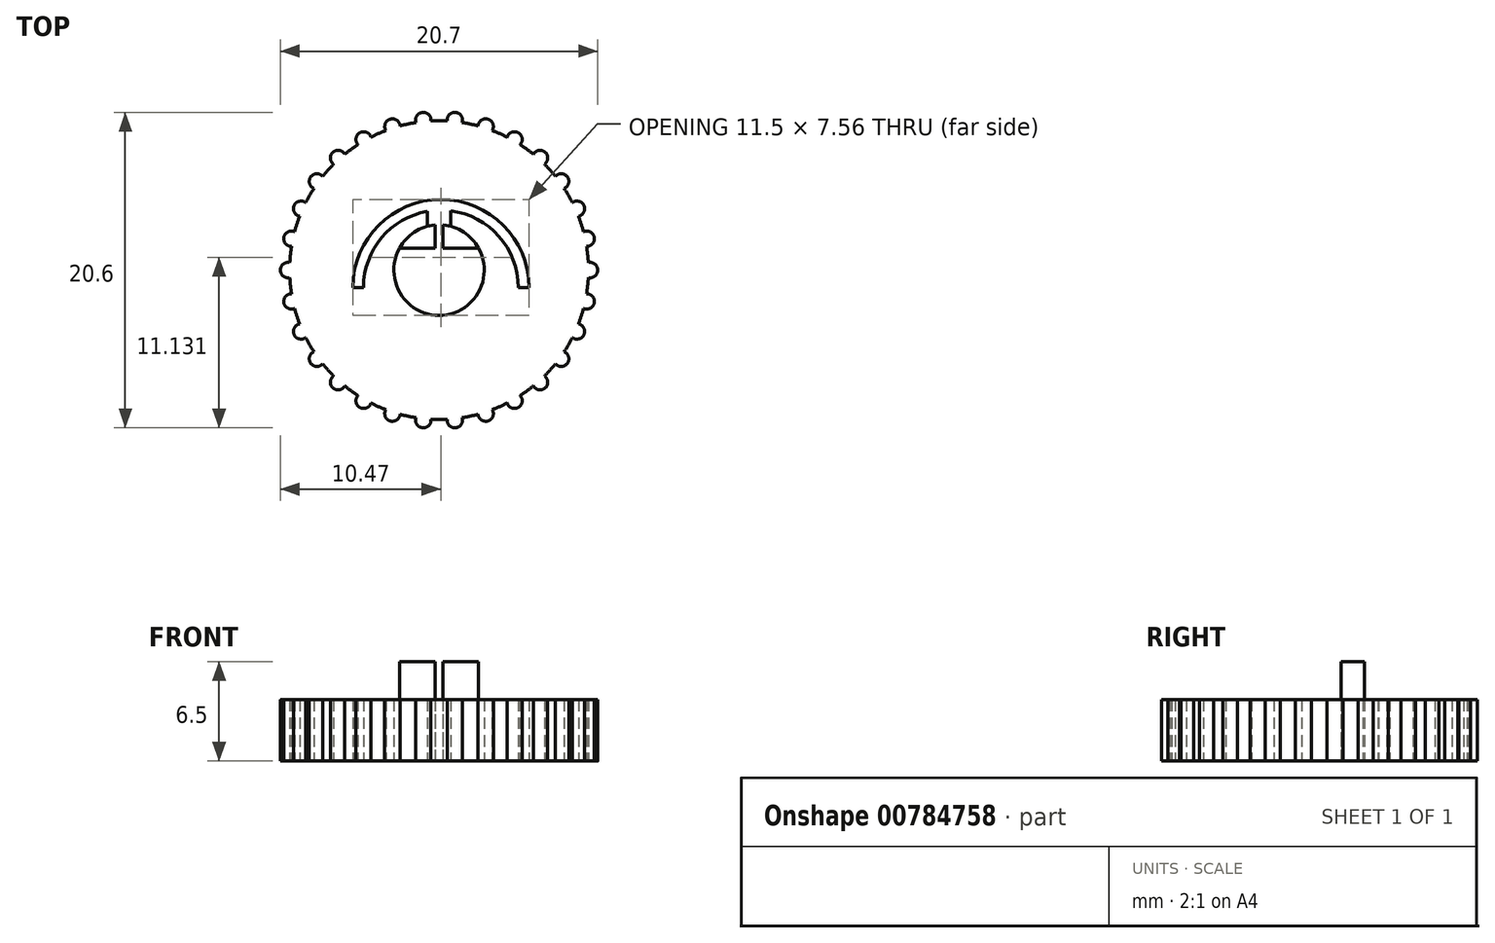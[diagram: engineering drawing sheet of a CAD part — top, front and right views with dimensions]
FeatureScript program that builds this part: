
annotation { "Feature Type Name" : "Feature", "Feature Type Description" : "" }
export const myFeature = defineFeature(function(context is Context, id is Id, definition is map)
    precondition{}
    {
        {
            var Q0;
            Q0=qCreatedBy(makeId("Top.planeOp"),FACE);
            var sketch = newSketch(context, id + "F0", { "sketchPlane" : qUnion([Q0])});
            skArc(sketch, "E0", {"start": v(-2.58, 1.43) * mm, "mid": v(0, -2.95) * mm, "end": v(2.58, 1.43) * mm});
            skArc(sketch, "E1", {"start": v(-0.75, 3.84) * mm, "mid": v(-3.75, 2.11) * mm, "end": v(-4.93, -1.14) * mm});
            skArc(sketch, "E2", {"start": v(5.87, -1.14) * mm, "mid": v(0.12, 4.61) * mm, "end": v(-5.63, -1.14) * mm});
            skArc(sketch, "E3", {"start": v(-9.74, -0.49) * mm, "mid": v(-9.7, -1.02) * mm, "end": v(-9.63, -1.55) * mm});
            skLineSegment(sketch, "E4", {"start": v(-5.63, -1.14) * mm, "end": v(-4.93, -1.14) * mm});
            skLineSegment(sketch, "E5.trimOffspring", {"start": v(5.17, -1.14) * mm, "end": v(5.87, -1.14) * mm});
            skArc(sketch, "E6.trimOffspring", {"start": v(5.17, -1.14) * mm, "mid": v(3.9, 2.2) * mm, "end": v(0.75, 3.87) * mm});
            skArc(sketch, "E7", {"start": v(-9.74, 0.49) * mm, "mid": v(-10.35, 0) * mm, "end": v(-9.74, -0.49) * mm});
            skArc(sketch, "E8.1.0", {"start": v(-9.63, -1.55) * mm, "mid": v(-10.12, -2.15) * mm, "end": v(-9.42, -2.5) * mm});
            skArc(sketch, "E8.2.0", {"start": v(-9.1, -3.52) * mm, "mid": v(-9.46, -4.21) * mm, "end": v(-8.7, -4.4) * mm});
            skArc(sketch, "E8.3.0", {"start": v(-8.16, -5.33) * mm, "mid": v(-8.37, -6.08) * mm, "end": v(-7.6, -6.12) * mm});
            skArc(sketch, "E8.4.0", {"start": v(-6.88, -6.91) * mm, "mid": v(-6.93, -7.7) * mm, "end": v(-6.15, -7.56) * mm});
            skArc(sketch, "E8.5.0", {"start": v(-5.3, -8.19) * mm, "mid": v(-5.18, -8.96) * mm, "end": v(-4.45, -8.68) * mm});
            skArc(sketch, "E8.6.0", {"start": v(-3.47, -9.11) * mm, "mid": v(-3.2, -9.84) * mm, "end": v(-2.55, -9.41) * mm});
            skArc(sketch, "E8.7.0", {"start": v(-1.5, -9.63) * mm, "mid": v(-1.08, -10.3) * mm, "end": v(-0.53, -9.74) * mm});
            skArc(sketch, "E8.8.0", {"start": v(0.53, -9.74) * mm, "mid": v(1.08, -10.3) * mm, "end": v(1.5, -9.63) * mm});
            skArc(sketch, "E8.9.0", {"start": v(2.55, -9.41) * mm, "mid": v(3.2, -9.84) * mm, "end": v(3.47, -9.11) * mm});
            skArc(sketch, "E8.10.0", {"start": v(4.45, -8.68) * mm, "mid": v(5.18, -8.96) * mm, "end": v(5.3, -8.19) * mm});
            skArc(sketch, "E8.11.0", {"start": v(6.15, -7.56) * mm, "mid": v(6.93, -7.7) * mm, "end": v(6.88, -6.91) * mm});
            skArc(sketch, "E8.12.0", {"start": v(7.6, -6.12) * mm, "mid": v(8.37, -6.08) * mm, "end": v(8.16, -5.33) * mm});
            skArc(sketch, "E8.13.0", {"start": v(8.7, -4.4) * mm, "mid": v(9.46, -4.21) * mm, "end": v(9.1, -3.52) * mm});
            skArc(sketch, "E8.14.0", {"start": v(9.42, -2.5) * mm, "mid": v(10.12, -2.15) * mm, "end": v(9.63, -1.55) * mm});
            skArc(sketch, "E8.15.0", {"start": v(9.74, -0.49) * mm, "mid": v(10.35, 0) * mm, "end": v(9.74, 0.49) * mm});
            skArc(sketch, "E8.16.0", {"start": v(9.63, 1.55) * mm, "mid": v(10.12, 2.15) * mm, "end": v(9.42, 2.5) * mm});
            skArc(sketch, "E8.17.0", {"start": v(9.1, 3.52) * mm, "mid": v(9.46, 4.21) * mm, "end": v(8.7, 4.4) * mm});
            skArc(sketch, "E8.18.0", {"start": v(8.16, 5.33) * mm, "mid": v(8.37, 6.08) * mm, "end": v(7.6, 6.12) * mm});
            skArc(sketch, "E8.19.0", {"start": v(6.88, 6.91) * mm, "mid": v(6.93, 7.7) * mm, "end": v(6.15, 7.56) * mm});
            skArc(sketch, "E8.20.0", {"start": v(5.3, 8.19) * mm, "mid": v(5.18, 8.96) * mm, "end": v(4.45, 8.68) * mm});
            skArc(sketch, "E8.21.0", {"start": v(3.47, 9.11) * mm, "mid": v(3.2, 9.84) * mm, "end": v(2.55, 9.41) * mm});
            skArc(sketch, "E8.22.0", {"start": v(1.5, 9.63) * mm, "mid": v(1.08, 10.3) * mm, "end": v(0.53, 9.74) * mm});
            skArc(sketch, "E8.23.0", {"start": v(-0.53, 9.74) * mm, "mid": v(-1.08, 10.3) * mm, "end": v(-1.5, 9.63) * mm});
            skArc(sketch, "E8.24.0", {"start": v(-2.55, 9.41) * mm, "mid": v(-3.2, 9.84) * mm, "end": v(-3.47, 9.11) * mm});
            skArc(sketch, "E8.25.0", {"start": v(-4.45, 8.68) * mm, "mid": v(-5.18, 8.96) * mm, "end": v(-5.3, 8.19) * mm});
            skArc(sketch, "E8.26.0", {"start": v(-6.15, 7.56) * mm, "mid": v(-6.93, 7.7) * mm, "end": v(-6.88, 6.91) * mm});
            skArc(sketch, "E8.27.0", {"start": v(-7.6, 6.12) * mm, "mid": v(-8.37, 6.08) * mm, "end": v(-8.16, 5.33) * mm});
            skArc(sketch, "E8.28.0", {"start": v(-8.7, 4.4) * mm, "mid": v(-9.46, 4.21) * mm, "end": v(-9.1, 3.52) * mm});
            skArc(sketch, "E8.29.0", {"start": v(-9.42, 2.5) * mm, "mid": v(-10.12, 2.15) * mm, "end": v(-9.63, 1.55) * mm});
            skArc(sketch, "E9.trimOffspring", {"start": v(-9.63, 1.55) * mm, "mid": v(-9.7, 1.02) * mm, "end": v(-9.74, 0.49) * mm});
            skArc(sketch, "E10.trimOffspring", {"start": v(-9.1, 3.52) * mm, "mid": v(-9.27, 3.01) * mm, "end": v(-9.42, 2.5) * mm});
            skArc(sketch, "E11.trimOffspring", {"start": v(-8.16, 5.33) * mm, "mid": v(-8.44, 4.88) * mm, "end": v(-8.7, 4.4) * mm});
            skArc(sketch, "E12.trimOffspring", {"start": v(-6.88, 6.91) * mm, "mid": v(-7.25, 6.52) * mm, "end": v(-7.6, 6.12) * mm});
            skArc(sketch, "E13.trimOffspring", {"start": v(-5.3, 8.19) * mm, "mid": v(-5.73, 7.89) * mm, "end": v(-6.15, 7.56) * mm});
            skArc(sketch, "E14.trimOffspring", {"start": v(-3.47, 9.11) * mm, "mid": v(-3.97, 8.9) * mm, "end": v(-4.45, 8.68) * mm});
            skArc(sketch, "E15.trimOffspring", {"start": v(-1.5, 9.63) * mm, "mid": v(-2.03, 9.54) * mm, "end": v(-2.55, 9.41) * mm});
            skArc(sketch, "E16.trimOffspring", {"start": v(0.53, 9.74) * mm, "mid": v(0, 9.75) * mm, "end": v(-0.53, 9.74) * mm});
            skArc(sketch, "E17.trimOffspring", {"start": v(2.55, 9.41) * mm, "mid": v(2.03, 9.54) * mm, "end": v(1.5, 9.63) * mm});
            skArc(sketch, "E18.trimOffspring", {"start": v(4.45, 8.68) * mm, "mid": v(3.97, 8.9) * mm, "end": v(3.47, 9.11) * mm});
            skArc(sketch, "E19.trimOffspring", {"start": v(6.15, 7.56) * mm, "mid": v(5.73, 7.89) * mm, "end": v(5.3, 8.19) * mm});
            skArc(sketch, "E20.trimOffspring", {"start": v(7.6, 6.12) * mm, "mid": v(7.25, 6.52) * mm, "end": v(6.88, 6.91) * mm});
            skArc(sketch, "E21.trimOffspring", {"start": v(8.7, 4.4) * mm, "mid": v(8.44, 4.87) * mm, "end": v(8.16, 5.33) * mm});
            skArc(sketch, "E22.trimOffspring", {"start": v(9.42, 2.5) * mm, "mid": v(9.27, 3.01) * mm, "end": v(9.1, 3.52) * mm});
            skArc(sketch, "E23.trimOffspring", {"start": v(9.74, 0.49) * mm, "mid": v(9.7, 1.02) * mm, "end": v(9.63, 1.55) * mm});
            skArc(sketch, "E24.trimOffspring", {"start": v(9.63, -1.55) * mm, "mid": v(9.7, -1.02) * mm, "end": v(9.74, -0.49) * mm});
            skArc(sketch, "E25.trimOffspring", {"start": v(8.16, -5.33) * mm, "mid": v(8.44, -4.87) * mm, "end": v(8.7, -4.4) * mm});
            skArc(sketch, "E26.trimOffspring", {"start": v(6.88, -6.91) * mm, "mid": v(7.25, -6.52) * mm, "end": v(7.6, -6.12) * mm});
            skArc(sketch, "E27.trimOffspring", {"start": v(5.3, -8.19) * mm, "mid": v(5.73, -7.89) * mm, "end": v(6.15, -7.56) * mm});
            skArc(sketch, "E28.trimOffspring", {"start": v(3.47, -9.11) * mm, "mid": v(3.97, -8.9) * mm, "end": v(4.45, -8.68) * mm});
            skArc(sketch, "E29.trimOffspring", {"start": v(1.5, -9.63) * mm, "mid": v(2.03, -9.54) * mm, "end": v(2.55, -9.41) * mm});
            skArc(sketch, "E30.trimOffspring", {"start": v(-0.53, -9.74) * mm, "mid": v(0, -9.75) * mm, "end": v(0.53, -9.74) * mm});
            skArc(sketch, "E31.trimOffspring", {"start": v(-2.55, -9.41) * mm, "mid": v(-2.03, -9.54) * mm, "end": v(-1.5, -9.63) * mm});
            skArc(sketch, "E32.trimOffspring", {"start": v(-4.45, -8.68) * mm, "mid": v(-3.97, -8.9) * mm, "end": v(-3.47, -9.11) * mm});
            skArc(sketch, "E33.trimOffspring", {"start": v(-6.15, -7.56) * mm, "mid": v(-5.73, -7.89) * mm, "end": v(-5.3, -8.19) * mm});
            skArc(sketch, "E34.trimOffspring", {"start": v(-7.6, -6.12) * mm, "mid": v(-7.25, -6.52) * mm, "end": v(-6.88, -6.91) * mm});
            skArc(sketch, "E35.trimOffspring", {"start": v(-8.7, -4.4) * mm, "mid": v(-8.44, -4.88) * mm, "end": v(-8.16, -5.33) * mm});
            skArc(sketch, "E36.trimOffspring", {"start": v(-9.42, -2.5) * mm, "mid": v(-9.27, -3.01) * mm, "end": v(-9.1, -3.52) * mm});
            skLineSegment(sketch, "E37.trimOffspring", {"start": v(-2.58, 1.43) * mm, "end": v(-0.75, 1.43) * mm});
            skLineSegment(sketch, "E38", {"start": v(-0.75, 3.84) * mm, "end": v(-0.75, 1.43) * mm});
            skLineSegment(sketch, "E39", {"start": v(0.75, 3.87) * mm, "end": v(0.75, 1.43) * mm});
            skLineSegment(sketch, "E40.trimOffspring", {"start": v(0.75, 1.43) * mm, "end": v(2.58, 1.43) * mm});
            skArc(sketch, "E41.trimOffspring", {"start": v(9.1, -3.52) * mm, "mid": v(9.27, -3.01) * mm, "end": v(9.42, -2.5) * mm});
            skSolve(sketch);
        }
        {
            var Q0;
            Q0=makeQuery(id+"F0.imprint","IMPRINT",FACE,{"disambiguationData":[TD([[makeQuery(id+"F0.imprint","IMPRINT",EDGE,{"derivedFrom":sQuery(id+"F0.wireOp",EDGE,"E0")}),-1.0]])]});
            extrude(context, id + "F1", {"entities" : qUnion([Q0]), "depth" : 4 * mm, "offsetDistance" : 25 * mm});
        }
        {
            var Q0;
            Q0=makeQuery(id+"F1.opExtrude","CAP_FACE",FACE,{"disambiguationData":[OSD([sQuery(id+"F0.wireOp",EDGE,"E0"),sQuery(id+"F0.wireOp",EDGE,"E1"),sQuery(id+"F0.wireOp",EDGE,"E2"),sQuery(id+"F0.wireOp",EDGE,"E3"),sQuery(id+"F0.wireOp",EDGE,"E4"),sQuery(id+"F0.wireOp",EDGE,"E5.trimOffspring"),sQuery(id+"F0.wireOp",EDGE,"E6.trimOffspring"),sQuery(id+"F0.wireOp",EDGE,"E7"),sQuery(id+"F0.wireOp",EDGE,"E8.1.0"),sQuery(id+"F0.wireOp",EDGE,"E8.2.0"),sQuery(id+"F0.wireOp",EDGE,"E8.3.0"),sQuery(id+"F0.wireOp",EDGE,"E8.4.0"),sQuery(id+"F0.wireOp",EDGE,"E8.5.0"),sQuery(id+"F0.wireOp",EDGE,"E8.6.0"),sQuery(id+"F0.wireOp",EDGE,"E8.7.0"),sQuery(id+"F0.wireOp",EDGE,"E8.8.0"),sQuery(id+"F0.wireOp",EDGE,"E8.9.0"),sQuery(id+"F0.wireOp",EDGE,"E8.10.0"),sQuery(id+"F0.wireOp",EDGE,"E8.11.0"),sQuery(id+"F0.wireOp",EDGE,"E8.12.0"),sQuery(id+"F0.wireOp",EDGE,"E8.14.0"),sQuery(id+"F0.wireOp",EDGE,"E8.15.0"),sQuery(id+"F0.wireOp",EDGE,"E8.16.0"),sQuery(id+"F0.wireOp",EDGE,"E8.17.0"),sQuery(id+"F0.wireOp",EDGE,"E8.18.0"),sQuery(id+"F0.wireOp",EDGE,"E8.19.0"),sQuery(id+"F0.wireOp",EDGE,"E8.20.0"),sQuery(id+"F0.wireOp",EDGE,"E8.21.0"),sQuery(id+"F0.wireOp",EDGE,"E8.22.0"),sQuery(id+"F0.wireOp",EDGE,"E8.23.0"),sQuery(id+"F0.wireOp",EDGE,"E8.24.0"),sQuery(id+"F0.wireOp",EDGE,"E8.25.0"),sQuery(id+"F0.wireOp",EDGE,"E8.26.0"),sQuery(id+"F0.wireOp",EDGE,"E8.27.0"),sQuery(id+"F0.wireOp",EDGE,"E8.28.0"),sQuery(id+"F0.wireOp",EDGE,"E8.29.0"),sQuery(id+"F0.wireOp",EDGE,"E9.trimOffspring"),sQuery(id+"F0.wireOp",EDGE,"E10.trimOffspring"),sQuery(id+"F0.wireOp",EDGE,"E11.trimOffspring"),sQuery(id+"F0.wireOp",EDGE,"E12.trimOffspring"),sQuery(id+"F0.wireOp",EDGE,"E13.trimOffspring"),sQuery(id+"F0.wireOp",EDGE,"E14.trimOffspring"),sQuery(id+"F0.wireOp",EDGE,"E15.trimOffspring"),sQuery(id+"F0.wireOp",EDGE,"E16.trimOffspring"),sQuery(id+"F0.wireOp",EDGE,"E17.trimOffspring"),sQuery(id+"F0.wireOp",EDGE,"E18.trimOffspring"),sQuery(id+"F0.wireOp",EDGE,"E19.trimOffspring"),sQuery(id+"F0.wireOp",EDGE,"E20.trimOffspring"),sQuery(id+"F0.wireOp",EDGE,"E21.trimOffspring"),sQuery(id+"F0.wireOp",EDGE,"E22.trimOffspring"),sQuery(id+"F0.wireOp",EDGE,"E23.trimOffspring"),sQuery(id+"F0.wireOp",EDGE,"E24.trimOffspring"),sQuery(id+"F0.wireOp",EDGE,"E25.trimOffspring"),sQuery(id+"F0.wireOp",EDGE,"E26.trimOffspring"),sQuery(id+"F0.wireOp",EDGE,"E27.trimOffspring"),sQuery(id+"F0.wireOp",EDGE,"E28.trimOffspring"),sQuery(id+"F0.wireOp",EDGE,"E29.trimOffspring"),sQuery(id+"F0.wireOp",EDGE,"E30.trimOffspring"),sQuery(id+"F0.wireOp",EDGE,"E31.trimOffspring"),sQuery(id+"F0.wireOp",EDGE,"E32.trimOffspring"),sQuery(id+"F0.wireOp",EDGE,"E33.trimOffspring"),sQuery(id+"F0.wireOp",EDGE,"E34.trimOffspring"),sQuery(id+"F0.wireOp",EDGE,"E35.trimOffspring"),sQuery(id+"F0.wireOp",EDGE,"E36.trimOffspring"),sQuery(id+"F0.wireOp",EDGE,"E37.trimOffspring"),sQuery(id+"F0.wireOp",EDGE,"E38"),sQuery(id+"F0.wireOp",EDGE,"E39"),sQuery(id+"F0.wireOp",EDGE,"E40.trimOffspring")])],"isStart":false});
            var sketch = newSketch(context, id + "F2", { "sketchPlane" : qUnion([Q0])});
            skArc(sketch, "E42", {"start": v(-0.25, 2.94) * mm, "mid": v(0, -2.95) * mm, "end": v(0.25, 2.94) * mm});
            skLineSegment(sketch, "E43", {"start": v(-0.75, 1.43) * mm, "end": v(-0.25, 1.43) * mm});
            skLineSegment(sketch, "E44", {"start": v(-0.25, 1.43) * mm, "end": v(-0.25, 2.94) * mm});
            skLineSegment(sketch, "E45", {"start": v(0.75, 1.43) * mm, "end": v(0.25, 1.43) * mm});
            skLineSegment(sketch, "E46", {"start": v(0.25, 1.43) * mm, "end": v(0.25, 2.94) * mm});
            skLineSegment(sketch, "E47", {"start": v(-0.75, 1.43) * mm, "end": v(-2.58, 1.43) * mm});
            skLineSegment(sketch, "E48", {"start": v(0.75, 1.43) * mm, "end": v(2.58, 1.43) * mm});
            skSolve(sketch);
        }
        {
            var Q0;
            {var subQ1=makeQuery(id+"F1.opExtrude","CAP_EDGE",EDGE,{"disambiguationData":[OSD([sQuery(id+"F0.wireOp",EDGE,"E37.trimOffspring")])],"isStart":false});Q0=makeQuery(id+"F2.imprint","IMPRINT",FACE,{"disambiguationData":[TD([[makeQuery(id+"F2.imprint","IMPRINT",EDGE,{"derivedFrom":subQ1}),1.0]])]});}
            var Q1;
            {var subQ1=makeQuery(id+"F1.opExtrude","CAP_EDGE",EDGE,{"disambiguationData":[OSD([sQuery(id+"F0.wireOp",EDGE,"E40.trimOffspring")])],"isStart":false});Q1=makeQuery(id+"F2.imprint","IMPRINT",FACE,{"disambiguationData":[TD([[makeQuery(id+"F2.imprint","IMPRINT",EDGE,{"derivedFrom":subQ1}),1.0]])]});}
            var Q2;
            {var subQ4=sQuery(id+"F2.wireOp",EDGE,"E43");Q2=makeQuery(id+"F2.imprint","IMPRINT",FACE,{"disambiguationData":[TD([[makeQuery(id+"F2.imprint","IMPRINT",EDGE,{"derivedFrom":subQ4}),1.0]])]});}
            var Q3;
            {var subQ0=sQuery(id+"F2.wireOp",EDGE,"E47");Q3=makeQuery(id+"F2.imprint","IMPRINT",FACE,{"disambiguationData":[TD([[makeQuery(id+"F2.imprint","IMPRINT",EDGE,{"derivedFrom":subQ0}),1.0]])]});}
            var Q4;
            {var subQ4=sQuery(id+"F2.wireOp",EDGE,"E45");Q4=makeQuery(id+"F2.imprint","IMPRINT",FACE,{"disambiguationData":[TD([[makeQuery(id+"F2.imprint","IMPRINT",EDGE,{"derivedFrom":subQ4}),-1.0]])]});}
            var Q5;
            {var subQ0=sQuery(id+"F2.wireOp",EDGE,"E48");Q5=makeQuery(id+"F2.imprint","IMPRINT",FACE,{"disambiguationData":[TD([[makeQuery(id+"F2.imprint","IMPRINT",EDGE,{"derivedFrom":subQ0}),1.0]])]});}
            extrude(context, id + "F3", {"entities" : qUnion([Q0, Q1, Q2, Q3, Q4, Q5]), "operationType" : NewBodyOperationType.ADD, "depth" : 2.5 * mm, "offsetDistance" : 25 * mm, "hasSecondDirection" : true, "secondDirectionOppositeDirection" : true, "secondDirectionDepth" : 4 * mm});
        }
    });
